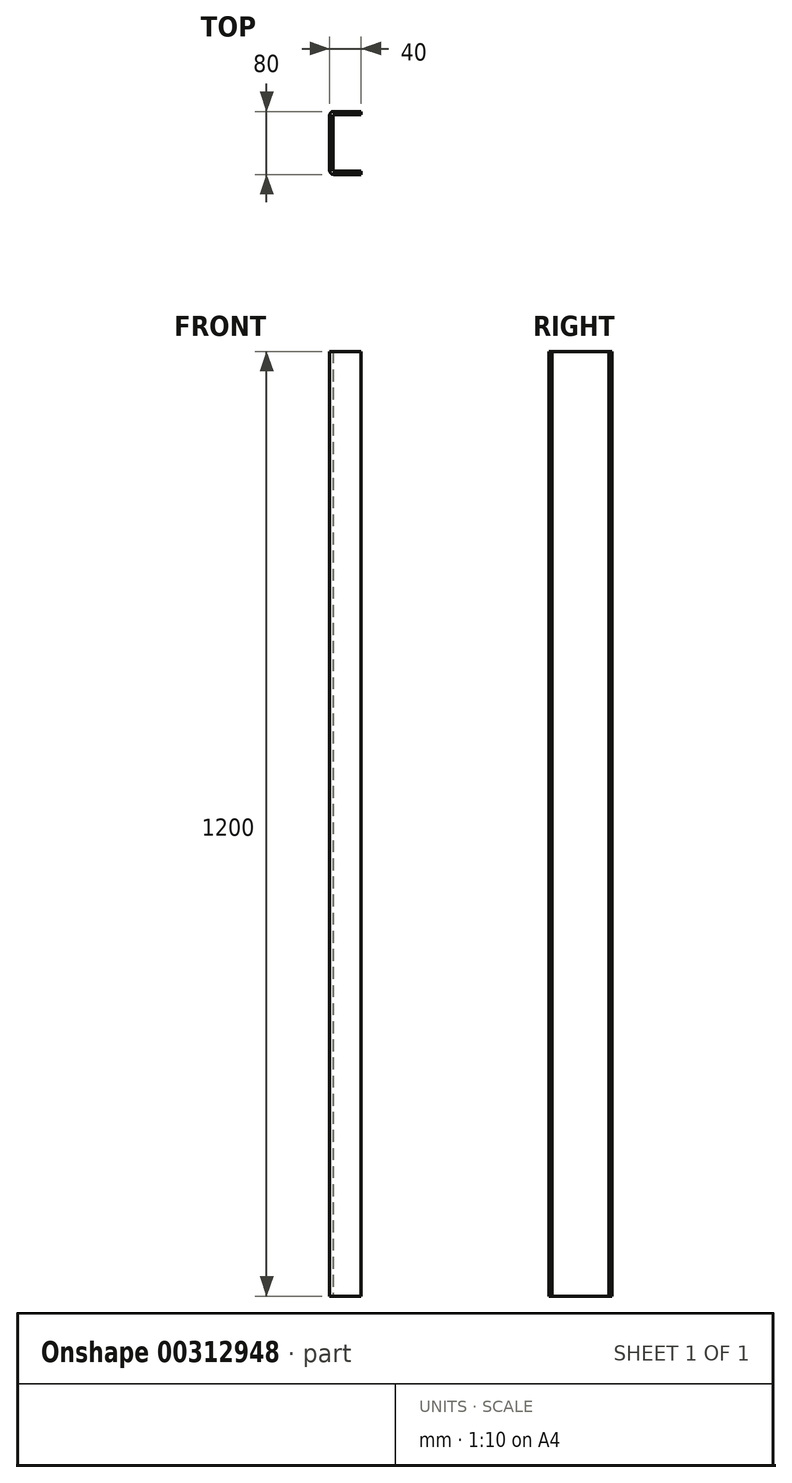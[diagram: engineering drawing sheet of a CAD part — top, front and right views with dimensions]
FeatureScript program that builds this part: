
annotation { "Feature Type Name" : "Feature", "Feature Type Description" : "" }
export const myFeature = defineFeature(function(context is Context, id is Id, definition is map)
    precondition{}
    {
        {
            var Q0;
            Q0=qCreatedBy(makeId("Top.planeOp"),FACE);
            var sketch = newSketch(context, id + "F0", { "sketchPlane" : qUnion([Q0])});
            skLineSegment(sketch, "E0.bottom", {"start": v(20, 40) * mm, "end": v(-20, 40) * mm});
            skLineSegment(sketch, "E0.top", {"start": v(20, -40) * mm, "end": v(-20, -40) * mm});
            skLineSegment(sketch, "E0.left", {"start": v(20, 40) * mm, "end": v(20, 36) * mm});
            skLineSegment(sketch, "E0.right", {"start": v(-20, 40) * mm, "end": v(-20, -40) * mm});
            skPoint(sketch, "E0.middle", {"position": v(0, 0) * mm});
            skLineSegment(sketch, "E1", {"start": v(20, -36) * mm, "end": v(-16, -36) * mm});
            skLineSegment(sketch, "E2", {"start": v(-16, -36) * mm, "end": v(-16, 36) * mm});
            skLineSegment(sketch, "E3", {"start": v(-16, 36) * mm, "end": v(20, 36) * mm});
            skLineSegment(sketch, "E4.trimOffspring", {"start": v(20, -36) * mm, "end": v(20, -40) * mm});
            skSolve(sketch);
        }
        {
            var Q0;
            Q0 = qSketchRegion(id + "F0", true);
            extrude(context, id + "F1", {"entities" : qUnion([Q0]), "depth" : 1200 * mm});
        }
        {
            var Q0;
            Q0=makeQuery(id+"F1.opExtrude","SWEPT_EDGE",EDGE,{"disambiguationData":[OSD([sQuery(id+"F0.wireOp",EDGE,"E0.bottom"),sQuery(id+"F0.wireOp",EDGE,"E0.right")])]});
            var Q1;
            Q1=makeQuery(id+"F1.opExtrude","SWEPT_EDGE",EDGE,{"disambiguationData":[OSD([sQuery(id+"F0.wireOp",EDGE,"E0.top"),sQuery(id+"F0.wireOp",EDGE,"E0.right")])]});
            fillet(context, id + "F2", {"entities" : qUnion([Q0, Q1]), "radius" : 5 * mm, "tangentPropagation" : true, "allowEdgeOverflow" : false});
        }
    });
